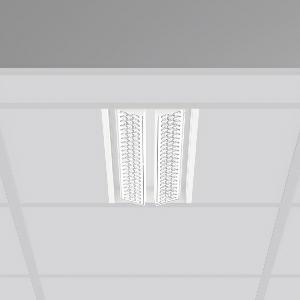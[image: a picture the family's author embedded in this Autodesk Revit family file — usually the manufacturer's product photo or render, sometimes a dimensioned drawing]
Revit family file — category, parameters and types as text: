
# Revit family: tx-move_901737_002_2_76_5734
name_source: partatom
category: Lighting Fixtures
units: mm (PartAtom-declared; Revit-internal decimal feet)

## family parameters
Cut with Voids When Loaded = No
Host = Face
Light Source = No
Part Type = Normal
Room Calculation Point = No
Round Connector Dimension = Use Diameter
Shared = No

## types (1)
- MultiLumen 1 (1 x LED Modul 927, 2025 lm, 2700)
    Apparent Load = 32 VA
    Approval mark = CE
    CIE Flux Codes = 77 96 99 100 100
    Color Rendering = 92
    Color Temperature = 2700
    Default Elevation = 1800 mm
    Description = Series: TX-MOVE
Einlege/Einbau-Flächenstrahler. Housing: sheet steel, powder-coated. 2xSwivel range: 90°. High-efficiency LED units with optimum light control thanks to clear plastic (PC) lens optics. Spezielle Mikrostrukturen reduzieren Gelbsaum. Symmetrical light distribution. Best colour rendering with CRI >90 for fresh products and coloured textiles. Suitable for laying in grid ceiling module 625. Connected converter included in separate gearbox.Suitable for through-wiring.MultiLumen: Luminous flux adjustable in 3 steps. Accessories: Mounting frame for installation in suspended ceilings. Environmentally friendly and resource-saving due to replaceable and recyclable components. 
Colour: traffic white, matt (RAL 9016)
Length: 622 mm
Width: 190 mm
Height: 39 mm
Cut-out length: 602 mm
Cut-out width: 174 mm
Recess height: 100 mm
Lamp: LED
Socket: without socket
Colour temperature: 2700K
Colour rendering index (CRI): 90
System power: 32 W
Rated luminous flux: 4050 lm
Luminous efficiency: 127 lm/W
System power 2: 43 W
Rated luminous flux 2: 5200 lm
Luminous efficiency 2: 121 lm/W
System power 3: 62 W
Rated luminous flux 3: 6850 lm
Luminous efficiency 3: 110 lm/W
Control gear: Dimmable EVG, DALI
Protection class: I
Type of protection: IP 20
    Height = 0 mm  [stored 0 ft]
    Lamp = 1 x LED Modul 927
    Lamp Light Flux = 2025 lm
    Lamp count = 1
    Length = 622 mm
    Lifetime = 50000 h
    Luminous efficacy = 127 lm/W
    Manufacturer = RZB
    ModVariant = No
    Model = 901737.002.2.76
    Mounting Place = Ceiling, Wall
    Mounting Type = Recessed
    Number of Poles = 1
    OnlyDefault = Yes
    Power Factor = 1
    Product Name = TX-MOVE
    Product group = Recessed projectors
    ProductGroupID = 401
    Protection Class = Protection class I
    Protection Degree = IP 20
    RLX_Detail_Level = 1
    RLX_Emergency_Light_Flux = 0 lm
    RLX_Emergency_Type = 0
    RLX_Emergency_Type_DB = No
    RlxData = <blob elided: 34133 chars, md5=19568467>
    Socket = socket
    Standby Power = 0 W
    System Light Flux = 4050 lm
    System Power = 32 W
    Type Comments = MultiLumen 1
    Type Image = 901737.002.jpg
    URL = http://relux.com
    VarID = multilumen_1
    Voltage = 230 V
    Voltage Range = 220-240 V
    Weight = 0.00 kg
    Width = 190 mm  [stored 0.62336 ft]

note: [stored X ft] marks values corroborated as IEEE doubles in the binary element streams (Revit-internal decimal feet)

## geometry (parser evidence)
native form markers: Blend x4, Sweep x17
no freeform markers — native parametric forms only
